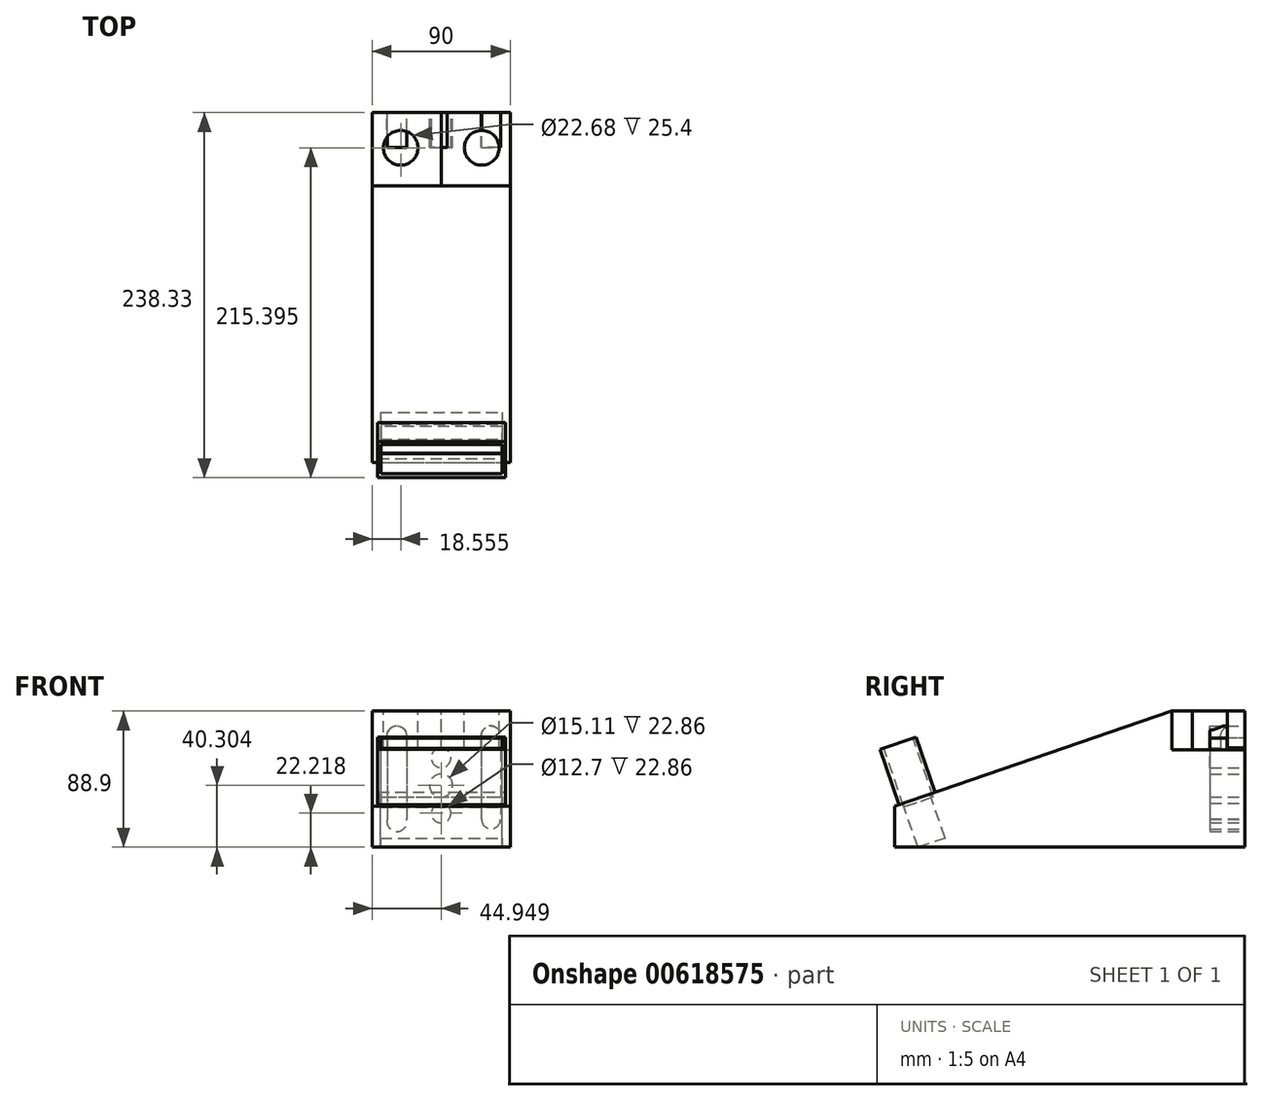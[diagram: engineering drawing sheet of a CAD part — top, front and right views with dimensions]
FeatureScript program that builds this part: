
annotation { "Feature Type Name" : "Feature", "Feature Type Description" : "" }
export const myFeature = defineFeature(function(context is Context, id is Id, definition is map)
    precondition{}
    {
        {
            var Q0;
            Q0=qCreatedBy(makeId("Top.planeOp"),FACE);
            var sketch = newSketch(context, id + "F0", { "sketchPlane" : qUnion([Q0])});
            skLineSegment(sketch, "E0.bottom", {"start": v(0, 0) * mm, "end": v(90, 0) * mm});
            skLineSegment(sketch, "E0.top", {"start": v(0, 228.6) * mm, "end": v(90, 228.6) * mm});
            skLineSegment(sketch, "E0.left", {"start": v(0, 0) * mm, "end": v(0, 228.6) * mm});
            skLineSegment(sketch, "E0.right", {"start": v(90, 0) * mm, "end": v(90, 228.6) * mm});
            skSolve(sketch);
        }
        {
            var Q0;
            Q0=qSketchRegion(id+"F0",true);
            extrude(context, id + "F1", {"entities" : qUnion([Q0]), "depth" : 88.9 * mm, "offsetDistance" : 25.4 * mm});
        }
        {
            var Q0;
            Q0=makeQuery(id+"F1.opExtrude","SWEPT_FACE",FACE,{"disambiguationData":[OSD([sQuery(id+"F0.wireOp",EDGE,"E0.right")])]});
            var sketch = newSketch(context, id + "F2", { "sketchPlane" : qUnion([Q0])});
            skLineSegment(sketch, "E1", {"start": v(180.72, 88.9) * mm, "end": v(0, 26.93) * mm});
            skSolve(sketch);
        }
        {
            var Q0;
            {var subQ0=sQuery(id+"F2.wireOp",EDGE,"E1");Q0=makeQuery(id+"F2.imprint","IMPRINT",FACE,{"disambiguationData":[TD([[makeQuery(id+"F2.imprint","IMPRINT",EDGE,{"derivedFrom":subQ0}),-1.0]])]});}
            extrude(context, id + "F3", {"entities" : qUnion([Q0]), "operationType" : NewBodyOperationType.REMOVE, "endBound" : BoundingType.UP_TO_NEXT, "oppositeDirection" : true, "depth" : 25.4 * mm, "offsetDistance" : 25.4 * mm});
        }
        {
            var Q0;
            Q0=makeQuery(id+"F3.boolean.opBoolean","COPY",FACE,{"derivedFrom":makeQuery(id+"F3.opExtrude","SWEPT_FACE",FACE,{"disambiguationData":[OSD([sQuery(id+"F2.wireOp",EDGE,"E1")])]})});
            var sketch = newSketch(context, id + "F4", { "sketchPlane" : qUnion([Q0])});
            skLineSegment(sketch, "E2.bottom", {"start": v(5.33, 33.01) * mm, "end": v(84.7, 33.01) * mm});
            skLineSegment(sketch, "E2.top", {"start": v(5.33, 14.27) * mm, "end": v(84.7, 14.27) * mm});
            skLineSegment(sketch, "E2.left", {"start": v(5.33, 33.01) * mm, "end": v(5.33, 14.27) * mm});
            skLineSegment(sketch, "E2.right", {"start": v(84.7, 33.01) * mm, "end": v(84.7, 14.27) * mm});
            skSolve(sketch);
        }
        {
            var Q0;
            Q0=qSketchRegion(id+"F4",true);
            extrude(context, id + "F5", {"entities" : qUnion([Q0]), "operationType" : NewBodyOperationType.REMOVE, "oppositeDirection" : true, "depth" : 30.48 * mm, "offsetDistance" : 25.4 * mm});
        }
        {
            var Q0;
            Q0=makeQuery(id+"F3.boolean.opBoolean","COPY",FACE,{"derivedFrom":makeQuery(id+"F3.opExtrude","SWEPT_FACE",FACE,{"disambiguationData":[OSD([sQuery(id+"F2.wireOp",EDGE,"E1")])]})});
            var sketch = newSketch(context, id + "F6", { "sketchPlane" : qUnion([Q0])});
            skLineSegment(sketch, "E3.bottom", {"start": v(3.52, 36.5) * mm, "end": v(87, 36.5) * mm});
            skLineSegment(sketch, "E3.top", {"start": v(3.52, 11.51) * mm, "end": v(87, 11.51) * mm});
            skLineSegment(sketch, "E3.left", {"start": v(3.52, 36.5) * mm, "end": v(3.52, 11.51) * mm});
            skLineSegment(sketch, "E3.right", {"start": v(87, 36.5) * mm, "end": v(87, 11.51) * mm});
            skSolve(sketch);
        }
        {
            var Q0;
            Q0=qSketchRegion(id+"F6",true);
            extrude(context, id + "F7", {"entities" : qUnion([Q0]), "operationType" : NewBodyOperationType.ADD, "depth" : 38.1 * mm, "offsetDistance" : 25.4 * mm});
        }
        {
            var Q0;
            Q0=makeQuery(id+"F7.opExtrude","CAP_FACE",FACE,{"disambiguationData":[OSD([sQuery(id+"F6.wireOp",EDGE,"E3.bottom"),sQuery(id+"F6.wireOp",EDGE,"E3.top"),sQuery(id+"F6.wireOp",EDGE,"E3.left"),sQuery(id+"F6.wireOp",EDGE,"E3.right")])],"isStart":false});
            var sketch = newSketch(context, id + "F8", { "sketchPlane" : qUnion([Q0])});
            skLineSegment(sketch, "E4.bottom", {"start": v(5.53, 34.4) * mm, "end": v(84.73, 34.4) * mm});
            skLineSegment(sketch, "E4.top", {"start": v(5.53, 14.14) * mm, "end": v(84.73, 14.14) * mm});
            skLineSegment(sketch, "E4.left", {"start": v(5.53, 34.4) * mm, "end": v(5.53, 14.14) * mm});
            skLineSegment(sketch, "E4.right", {"start": v(84.73, 34.4) * mm, "end": v(84.73, 14.14) * mm});
            skSolve(sketch);
        }
        {
            var Q0;
            Q0=qSketchRegion(id+"F8",true);
            extrude(context, id + "F9", {"entities" : qUnion([Q0]), "operationType" : NewBodyOperationType.REMOVE, "oppositeDirection" : true, "depth" : 40.64 * mm, "offsetDistance" : 25.4 * mm});
        }
        {
            var Q0;
            Q0=makeQuery(id+"F1.opExtrude","CAP_FACE",FACE,{"disambiguationData":[OSD([sQuery(id+"F0.wireOp",EDGE,"E0.bottom"),sQuery(id+"F0.wireOp",EDGE,"E0.top"),sQuery(id+"F0.wireOp",EDGE,"E0.left"),sQuery(id+"F0.wireOp",EDGE,"E0.right")])],"isStart":false});
            var sketch = newSketch(context, id + "F10", { "sketchPlane" : qUnion([Q0])});
            skCircle(sketch, "E5", {"center": v(18.56, 205.66) * mm, "radius": 11.34 * mm});
            skLineSegment(sketch, "E6", {"start": v(45, 228.6) * mm, "end": v(45, 180.72) * mm});
            skCircle(sketch, "E7.MirrorC", {"center": v(71.45, 205.66) * mm, "radius": 11.34 * mm});
            skSolve(sketch);
        }
        {
            var Q0;
            Q0=makeQuery(id+"F10.imprint","IMPRINT",FACE,{"disambiguationData":[TD([[makeQuery(id+"F10.imprint","IMPRINT",EDGE,{"derivedFrom":sQuery(id+"F10.wireOp",EDGE,"E5")}),1.0]])]});
            var Q1;
            Q1=makeQuery(id+"F10.imprint","IMPRINT",FACE,{"disambiguationData":[TD([[makeQuery(id+"F10.imprint","IMPRINT",EDGE,{"derivedFrom":sQuery(id+"F10.wireOp",EDGE,"E7.MirrorC")}),-1.0]])]});
            extrude(context, id + "F11", {"entities" : qUnion([Q0, Q1]), "operationType" : NewBodyOperationType.REMOVE, "oppositeDirection" : true, "depth" : 25.4 * mm, "offsetDistance" : 25.4 * mm});
        }
        {
            var Q0;
            Q0=makeQuery(id+"F1.opExtrude","SWEPT_FACE",FACE,{"disambiguationData":[OSD([sQuery(id+"F0.wireOp",EDGE,"E0.top")])]});
            var sketch = newSketch(context, id + "F12", { "sketchPlane" : qUnion([Q0])});
            skLineSegment(sketch, "E8.top", {"start": v(-83.85, 18.12) * mm, "end": v(-83.64, 18.12) * mm});
            skLineSegment(sketch, "E8.left", {"start": v(-83.85, 72.72) * mm, "end": v(-83.85, 18.12) * mm});
            skLineSegment(sketch, "E8.right", {"start": v(-71.23, 72.72) * mm, "end": v(-71.23, 18.12) * mm});
            skArc(sketch, "E9", {"start": v(-71.23, 71.4) * mm, "mid": v(-77.54, 79.17) * mm, "end": v(-83.85, 71.4) * mm});
            skArc(sketch, "E10", {"start": v(-83.64, 18.12) * mm, "mid": v(-77.54, 12.03) * mm, "end": v(-71.44, 18.12) * mm});
            skLineSegment(sketch, "E11.trimOffspring", {"start": v(-71.44, 18.12) * mm, "end": v(-71.23, 18.12) * mm});
            skCircle(sketch, "E12", {"center": v(-44.95, 58.4) * mm, "radius": 6.38 * mm});
            skCircle(sketch, "E13", {"center": v(-44.95, 40.3) * mm, "radius": 7.55 * mm});
            skCircle(sketch, "E14", {"center": v(-44.95, 22.22) * mm, "radius": 6.35 * mm});
            skLineSegment(sketch, "E15.left", {"start": v(-22.43, 72.72) * mm, "end": v(-22.43, 16.76) * mm});
            skLineSegment(sketch, "E15.right", {"start": v(-9.8, 72.72) * mm, "end": v(-9.8, 16.76) * mm});
            skArc(sketch, "E16", {"start": v(-9.8, 71.54) * mm, "mid": v(-16.11, 79.15) * mm, "end": v(-22.43, 71.54) * mm});
            skArc(sketch, "E17", {"start": v(-22.43, 18.46) * mm, "mid": v(-16.11, 10.22) * mm, "end": v(-9.8, 18.46) * mm});
            skSolve(sketch);
        }
        {
            var Q0;
            Q0=qSketchRegion(id+"F12",true);
            extrude(context, id + "F13", {"entities" : qUnion([Q0]), "operationType" : NewBodyOperationType.REMOVE, "oppositeDirection" : true, "depth" : 22.86 * mm, "offsetDistance" : 25.4 * mm});
        }
    });
